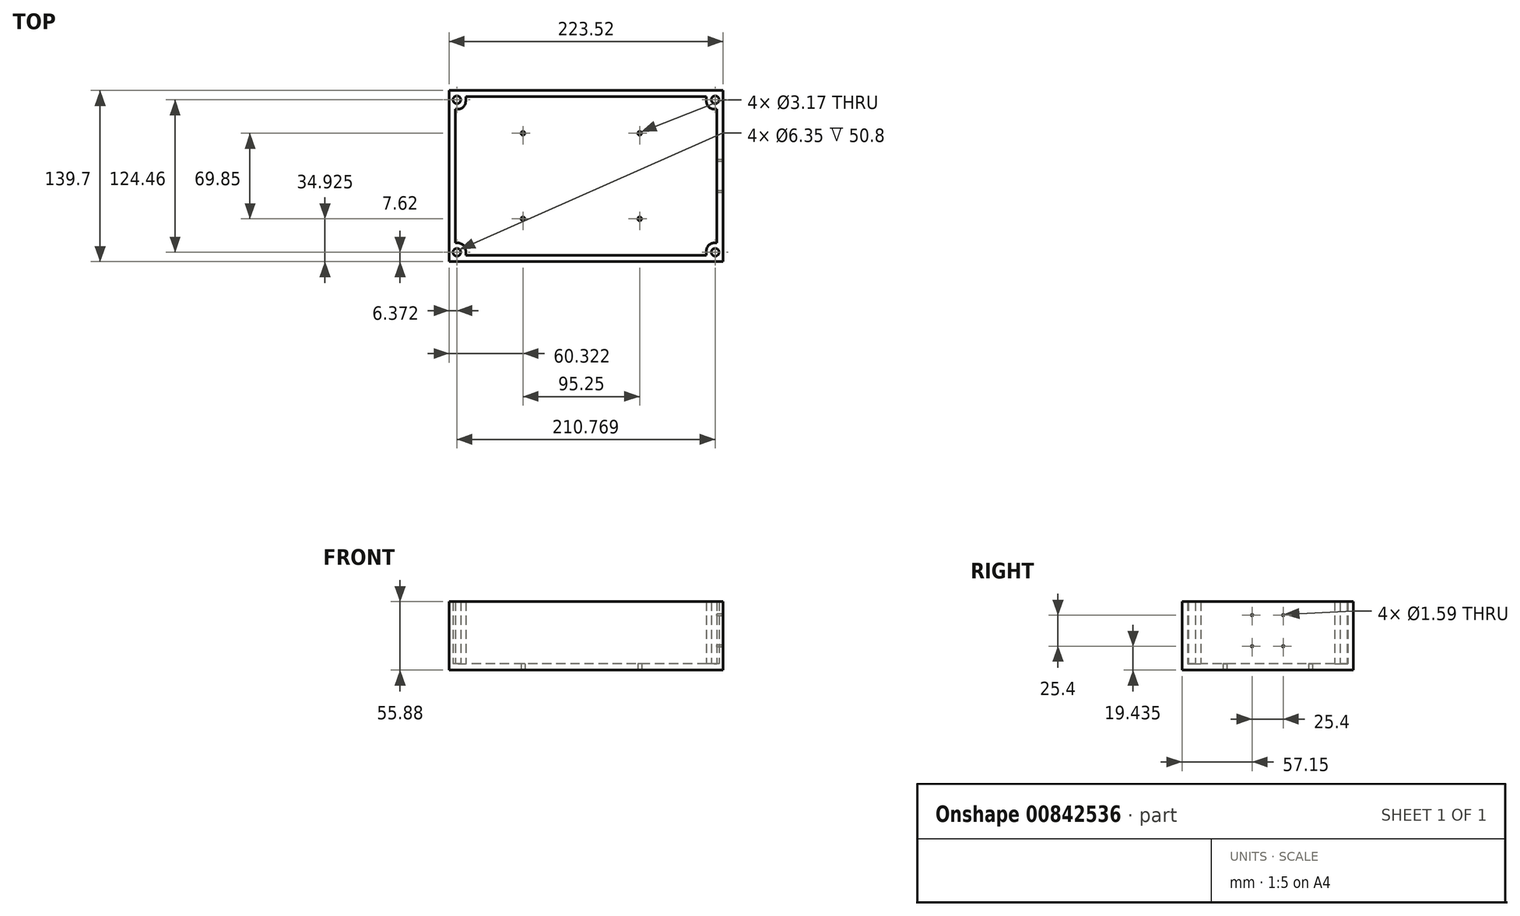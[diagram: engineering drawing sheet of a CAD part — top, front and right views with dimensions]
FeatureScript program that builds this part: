
annotation { "Feature Type Name" : "Feature", "Feature Type Description" : "" }
export const myFeature = defineFeature(function(context is Context, id is Id, definition is map)
    precondition{}
    {
        {
            var Q0;
            Q0=qCreatedBy(makeId("Top.planeOp"),FACE);
            var sketch = newSketch(context, id + "F0", { "sketchPlane" : qUnion([Q0])});
            skLineSegment(sketch, "E0.bottom", {"start": v(-237.1, 139.7) * mm, "end": v(-13.58, 139.7) * mm});
            skLineSegment(sketch, "E0.top", {"start": v(-237.1, 0) * mm, "end": v(-13.58, 0) * mm});
            skLineSegment(sketch, "E0.left", {"start": v(-237.1, 139.7) * mm, "end": v(-237.1, 0) * mm});
            skLineSegment(sketch, "E0.right", {"start": v(-13.58, 139.7) * mm, "end": v(-13.58, 0) * mm});
            skCircle(sketch, "E1", {"center": v(-176.78, 104.78) * mm, "radius": 1.59 * mm});
            skCircle(sketch, "E2.MirrorC", {"center": v(-81.53, 104.78) * mm, "radius": 1.59 * mm});
            skCircle(sketch, "E3.MirrorC", {"center": v(-176.78, 34.92) * mm, "radius": 1.59 * mm});
            skCircle(sketch, "E4.MirrorC", {"center": v(-81.53, 34.92) * mm, "radius": 1.59 * mm});
            skSolve(sketch);
        }
        {
            var Q0;
            Q0=qSketchRegion(id+"F0",true);
            extrude(context, id + "F1", {"entities" : qUnion([Q0]), "depth" : 5.08 * mm});
        }
        {
            var Q0;
            Q0=makeQuery(id+"F1.opExtrude","CAP_FACE",FACE,{"disambiguationData":[OSD([sQuery(id+"F0.wireOp",EDGE,"E0.bottom"),sQuery(id+"F0.wireOp",EDGE,"E0.top"),sQuery(id+"F0.wireOp",EDGE,"E0.left"),sQuery(id+"F0.wireOp",EDGE,"E0.right")])],"isStart":false});
            var sketch = newSketch(context, id + "F2", { "sketchPlane" : qUnion([Q0])});
            skLineSegment(sketch, "E5.bottom", {"start": v(-237.1, 139.7) * mm, "end": v(-229.48, 139.7) * mm});
            skLineSegment(sketch, "E5.left", {"start": v(-237.1, 139.7) * mm, "end": v(-237.1, 132.08) * mm});
            skCircle(sketch, "E6", {"center": v(-230.73, 132.08) * mm, "radius": 3.17 * mm});
            skLineSegment(sketch, "E7.bottom", {"start": v(-237.1, 139.7) * mm, "end": v(-221.86, 139.7) * mm});
            skLineSegment(sketch, "E7.left", {"start": v(-237.1, 139.7) * mm, "end": v(-237.1, 124.46) * mm});
            skLineSegment(sketch, "E8.left", {"start": v(-237.1, 124.46) * mm, "end": v(-237.1, 0) * mm});
            skLineSegment(sketch, "E9", {"start": v(-232.02, 124.46) * mm, "end": v(-232.02, 15.24) * mm});
            skLineSegment(sketch, "E10.bottom", {"start": v(-125.34, 134.62) * mm, "end": v(-223.55, 134.62) * mm});
            skLineSegment(sketch, "E10.top", {"start": v(-125.34, 139.7) * mm, "end": v(-221.86, 139.7) * mm});
            skLineSegment(sketch, "E11", {"start": v(-223.55, 134.62) * mm, "end": v(-223.55, 130.81) * mm});
            skLineSegment(sketch, "E12", {"start": v(-229.9, 124.46) * mm, "end": v(-232.02, 124.46) * mm});
            skPoint(sketch, "E13.visualSharp", {"position": v(-223.55, 124.46) * mm});
            skArc(sketch, "E13.filletArc", {"start": v(-229.9, 124.46) * mm, "mid": v(-225.41, 126.32) * mm, "end": v(-223.55, 130.81) * mm});
            skLineSegment(sketch, "E14.MirrorCS", {"start": v(-27.13, 134.62) * mm, "end": v(-27.13, 130.81) * mm});
            skLineSegment(sketch, "E15.MirrorCS", {"start": v(-13.58, 139.7) * mm, "end": v(-28.82, 139.7) * mm});
            skLineSegment(sketch, "E16.MirrorCS", {"start": v(-13.58, 139.7) * mm, "end": v(-21.2, 139.7) * mm});
            skLineSegment(sketch, "E17.MirrorCS", {"start": v(-20.78, 124.46) * mm, "end": v(-18.66, 124.46) * mm});
            skCircle(sketch, "E18.MirrorC", {"center": v(-19.96, 132.08) * mm, "radius": 3.17 * mm});
            skLineSegment(sketch, "E19.MirrorCS", {"start": v(-13.58, 139.7) * mm, "end": v(-13.58, 132.08) * mm});
            skLineSegment(sketch, "E20.MirrorCS", {"start": v(-13.58, 139.7) * mm, "end": v(-13.58, 124.46) * mm});
            skArc(sketch, "E21.MirrorCS", {"start": v(-20.78, 124.46) * mm, "mid": v(-25.27, 126.32) * mm, "end": v(-27.13, 130.81) * mm});
            skPoint(sketch, "E22.MirrorP", {"position": v(-27.13, 124.46) * mm});
            skLineSegment(sketch, "E23.MirrorCS", {"start": v(-13.58, 124.46) * mm, "end": v(-13.58, 0) * mm});
            skLineSegment(sketch, "E24.MirrorCS", {"start": v(-125.34, 134.62) * mm, "end": v(-27.13, 134.62) * mm});
            skLineSegment(sketch, "E25.MirrorCS", {"start": v(-125.34, 139.7) * mm, "end": v(-28.82, 139.7) * mm});
            skLineSegment(sketch, "E26.MirrorCS", {"start": v(-18.66, 124.46) * mm, "end": v(-18.66, 15.24) * mm});
            skLineSegment(sketch, "E27.MirrorCS", {"start": v(-20.78, 15.24) * mm, "end": v(-18.66, 15.24) * mm});
            skLineSegment(sketch, "E28.MirrorCS", {"start": v(-229.9, 15.24) * mm, "end": v(-232.02, 15.24) * mm});
            skLineSegment(sketch, "E29.MirrorCS", {"start": v(-27.13, 5.08) * mm, "end": v(-27.13, 8.89) * mm});
            skLineSegment(sketch, "E30.MirrorCS", {"start": v(-223.55, 5.08) * mm, "end": v(-223.55, 8.89) * mm});
            skArc(sketch, "E31.MirrorCS", {"start": v(-20.78, 15.24) * mm, "mid": v(-25.27, 13.38) * mm, "end": v(-27.13, 8.89) * mm});
            skCircle(sketch, "E32.MirrorC", {"center": v(-19.96, 7.62) * mm, "radius": 3.17 * mm});
            skLineSegment(sketch, "E33.MirrorCS", {"start": v(-237.1, 0) * mm, "end": v(-221.86, 0) * mm});
            skLineSegment(sketch, "E34.MirrorCS", {"start": v(-13.58, 0) * mm, "end": v(-13.58, 15.24) * mm});
            skLineSegment(sketch, "E35.MirrorCS", {"start": v(-237.1, 0) * mm, "end": v(-237.1, 15.24) * mm});
            skLineSegment(sketch, "E36.MirrorCS", {"start": v(-13.58, 0) * mm, "end": v(-13.58, 7.62) * mm});
            skLineSegment(sketch, "E37.MirrorCS", {"start": v(-13.58, 0) * mm, "end": v(-21.2, 0) * mm});
            skLineSegment(sketch, "E38.MirrorCS", {"start": v(-237.1, 0) * mm, "end": v(-229.48, 0) * mm});
            skLineSegment(sketch, "E39.MirrorCS", {"start": v(-237.1, 0) * mm, "end": v(-237.1, 7.62) * mm});
            skArc(sketch, "E40.MirrorCS", {"start": v(-229.9, 15.24) * mm, "mid": v(-225.41, 13.38) * mm, "end": v(-223.55, 8.89) * mm});
            skLineSegment(sketch, "E41.MirrorCS", {"start": v(-13.58, 0) * mm, "end": v(-28.82, 0) * mm});
            skCircle(sketch, "E42.MirrorC", {"center": v(-230.73, 7.62) * mm, "radius": 3.17 * mm});
            skLineSegment(sketch, "E43.MirrorCS", {"start": v(-125.34, 5.08) * mm, "end": v(-27.13, 5.08) * mm});
            skLineSegment(sketch, "E44.MirrorCS", {"start": v(-125.34, 5.08) * mm, "end": v(-223.55, 5.08) * mm});
            skPoint(sketch, "E45.MirrorP", {"position": v(-27.13, 15.24) * mm});
            skLineSegment(sketch, "E46.MirrorCS", {"start": v(-125.34, 0) * mm, "end": v(-221.86, 0) * mm});
            skLineSegment(sketch, "E47.MirrorCS", {"start": v(-125.34, 0) * mm, "end": v(-28.82, 0) * mm});
            skPoint(sketch, "E48.MirrorP", {"position": v(-223.55, 15.24) * mm});
            skSolve(sketch);
        }
        {
            var Q0;
            Q0=qSketchRegion(id+"F2",true);
            extrude(context, id + "F3", {"entities" : qUnion([Q0]), "operationType" : NewBodyOperationType.ADD, "depth" : 50.8 * mm});
        }
        {
            var Q0;
            Q0=makeQuery(id+"F3.opExtrude","SWEPT_FACE",FACE,{"disambiguationData":[OSD([sQuery(id+"F2.wireOp",EDGE,"E26.MirrorCS")])]});
            var sketch = newSketch(context, id + "F4", { "sketchPlane" : qUnion([Q0])});
            skCircle(sketch, "E49", {"center": v(-82.55, 44.83) * mm, "radius": 0.8 * mm});
            skCircle(sketch, "E50", {"center": v(-57.15, 44.83) * mm, "radius": 0.8 * mm});
            skCircle(sketch, "E51", {"center": v(-82.55, 19.43) * mm, "radius": 0.8 * mm});
            skCircle(sketch, "E52", {"center": v(-57.15, 19.43) * mm, "radius": 0.8 * mm});
            skLineSegment(sketch, "E53", {"start": v(-69.85, 55.88) * mm, "end": v(-69.85, 5.08) * mm});
            skSolve(sketch);
        }
        {
            var Q0;
            Q0 = qSketchRegion(id + "F4", true);
            extrude(context, id + "F5", {"entities" : qUnion([Q0]), "operationType" : NewBodyOperationType.REMOVE, "oppositeDirection" : true, "depth" : 51.56 * mm, "offsetDistance" : 25.4 * mm});
        }
    });
